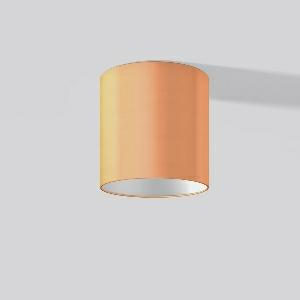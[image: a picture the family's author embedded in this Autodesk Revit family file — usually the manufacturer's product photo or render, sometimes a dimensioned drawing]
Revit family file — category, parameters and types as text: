
# Revit family: toledo_flatliner_901628_002_fee1
name_source: partatom
category: Lighting Fixtures
units: mm (PartAtom-declared; Revit-internal decimal feet)

## family parameters
Cut with Voids When Loaded = No
Host = Face
Light Source = No
Part Type = Normal
Room Calculation Point = No
Round Connector Dimension = Use Diameter
Shared = No

## types (1)
- 982299.002 (1 x LED Modul 830, 310 lm, 3000)
    Apparent Load = 5 VA
    CIE Flux Codes = 56 78 92 81 100
    Color Rendering = 80
    Color Temperature = 3000
    Default Elevation = 1800 mm
    Description = Series: TOLEDO FLATLINER
Decorative ceiling luminaire for interior decoration. Base luminaire prepared for the installation of fabric lampshade. Cylinder housing sheet steel, powder-coated. Housing: die cast aluminium and sheet steel, powder-coated. Bezel ring: die-cast aluminium, powder-coated. Lightguide and diffuser made of non-yellowing plastic (PMMA) opal matt. Modular design: With the basic luminaire, a square or cylindrical fabric lampshade must always be ordered separately. Fabric lampshades can be fitted to the basic luminaire without tools. Order satin finish diffuser as separate accessory. 
Colour: white
Diameter: 160 mm
Height: 65 mm
Lamp: LED
Socket: without socket
Colour temperature: 3000K
Colour rendering index (CRI): 80
System power: 5 W
Rated luminous flux: 310 lm
Luminous efficiency: 62 lm/W
Control gear: Regulated power supply
Protection class: II
Type of protection: IP 40
    Height = 65 mm
    Lamp = 1 x LED Modul 830
    Lamp Light Flux = 310 lm
    Lamp count = 1
    Length = 160 mm
    Lifetime = 50000 h
    Luminous efficacy = 62 lm/W
    Manufacturer = RZB
    ModVariant = No
    Model = 901628.002
    Mounting Place = Ceiling
    Mounting Type = Surface mounted
    Number of Poles = 1
    OnlyDefault = Yes
    Power Factor = 1
    Product Name = TOLEDO FLATLINER
    Product group = Surface mounted ceiling Fabric lampshade luminaires
    ProductGroupID = 313
    Protection Class = Protection class II
    Protection Degree = IP 40
    RLX_Detail_Level = 1
    RLX_Emergency_Light_Flux = 0 lm
    RLX_Emergency_Type = 0
    RLX_Emergency_Type_DB = No
    RlxData = <blob elided: 62289 chars, md5=2723af88>
    Socket = socket
    Standby Power = 0 W
    System Light Flux = 310 lm
    System Power = 5 W
    Type Image = toledo_flatliner_anbau_rund_orange_odeckel.jpg
    URL = http://relux.com
    VarID = 982299_002_f7b2
    Voltage = 230 V
    Voltage Range = 220-240 V
    Weight = 0.00 kg
    Width = 0 mm  [stored 0 ft]

note: [stored X ft] marks values corroborated as IEEE doubles in the binary element streams (Revit-internal decimal feet)

## geometry (parser evidence)
native form markers: Blend x4, Sweep x11
no freeform markers — native parametric forms only
